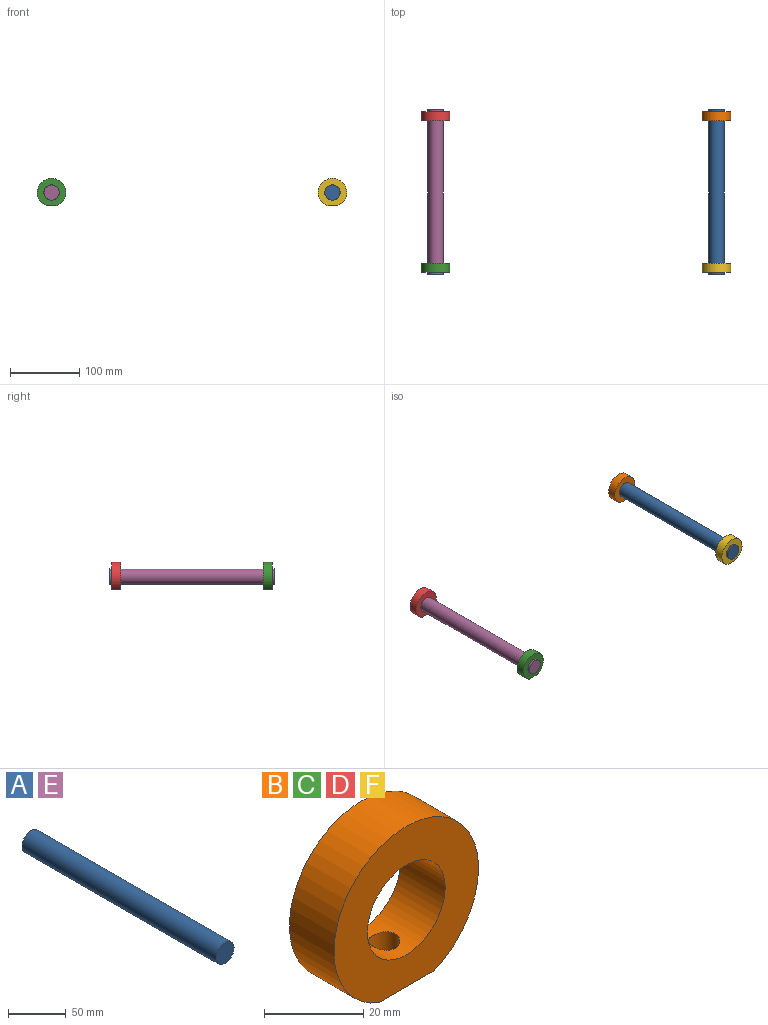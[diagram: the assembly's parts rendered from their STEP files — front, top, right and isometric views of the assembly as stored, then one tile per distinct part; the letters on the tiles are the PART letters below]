
ASSEMBLY  parts=6 mates=5
PART A: 3 faces, bbox 22x238.1x22 mm
  f0: cylinder r=11mm len=238.13mm, axis (0,1,0), area 16455.3mm2, adj f1,f2
  f1: plane 22x22mm, normal (0,-1,0), area 380mm2, adj f0
  f2: plane 22x22mm, normal (0,1,0), area 380mm2, adj f0
PART B: 6 faces, bbox 41.3x12.7x39.7 mm
  f0: cylinder r=11.11mm len=22.23mm, axis (0,1,0), area 854.7mm2, adj f2,f3,f5
  f1: cylinder r=20.64mm len=41.28mm, axis (0,1,0), area 1439.9mm2, adj f2,f3,f4
  f2: plane 41.28x39.69mm, normal (0,-1,0), area 933.1mm2, adj f0,f1,f4
  f3: plane 41.28x39.69mm, normal (0,1,0), area 933.1mm2, adj f0,f1,f4
  f4: plane 15.88x12.7mm, normal (0,0,-1), area 169.9mm2, adj f1,f2,f3,f5
  f5: cylinder r=3.17mm len=8.4mm, axis (0,0,-1), area 162.9mm2, adj f0,f4
PART C: same geometry as B
PART D: same geometry as B
PART E: same geometry as A
PART F: same geometry as B
PLACE A t=(111.78,0,73.65)mm
PLACE B t=(111.78,109.54,73.65)mm
PLACE C t=(-294.62,-109.54,73.65)mm
PLACE D t=(-294.62,109.54,73.65)mm
PLACE E t=(-294.62,0,73.65)mm fixed
PLACE F t=(111.78,-109.54,73.65)mm
MATE fastened F.f0 <-> A.f0  axis (0,-1,0) through (111.78,-115.89,73.65)mm
MATE fastened A.f0 <-> E.f1  axis (0,-1,0) through (111.78,-119.06,73.65)mm
MATE fastened D.f0 <-> E.f0  axis (0,1,0) through (-294.62,115.89,73.65)mm
MATE fastened C.f1 <-> E.f0  axis (0,-1,0) through (-294.62,-115.89,73.65)mm
MATE fastened B.f0 <-> A.f0  axis (0,1,0) through (111.78,115.89,73.65)mm
